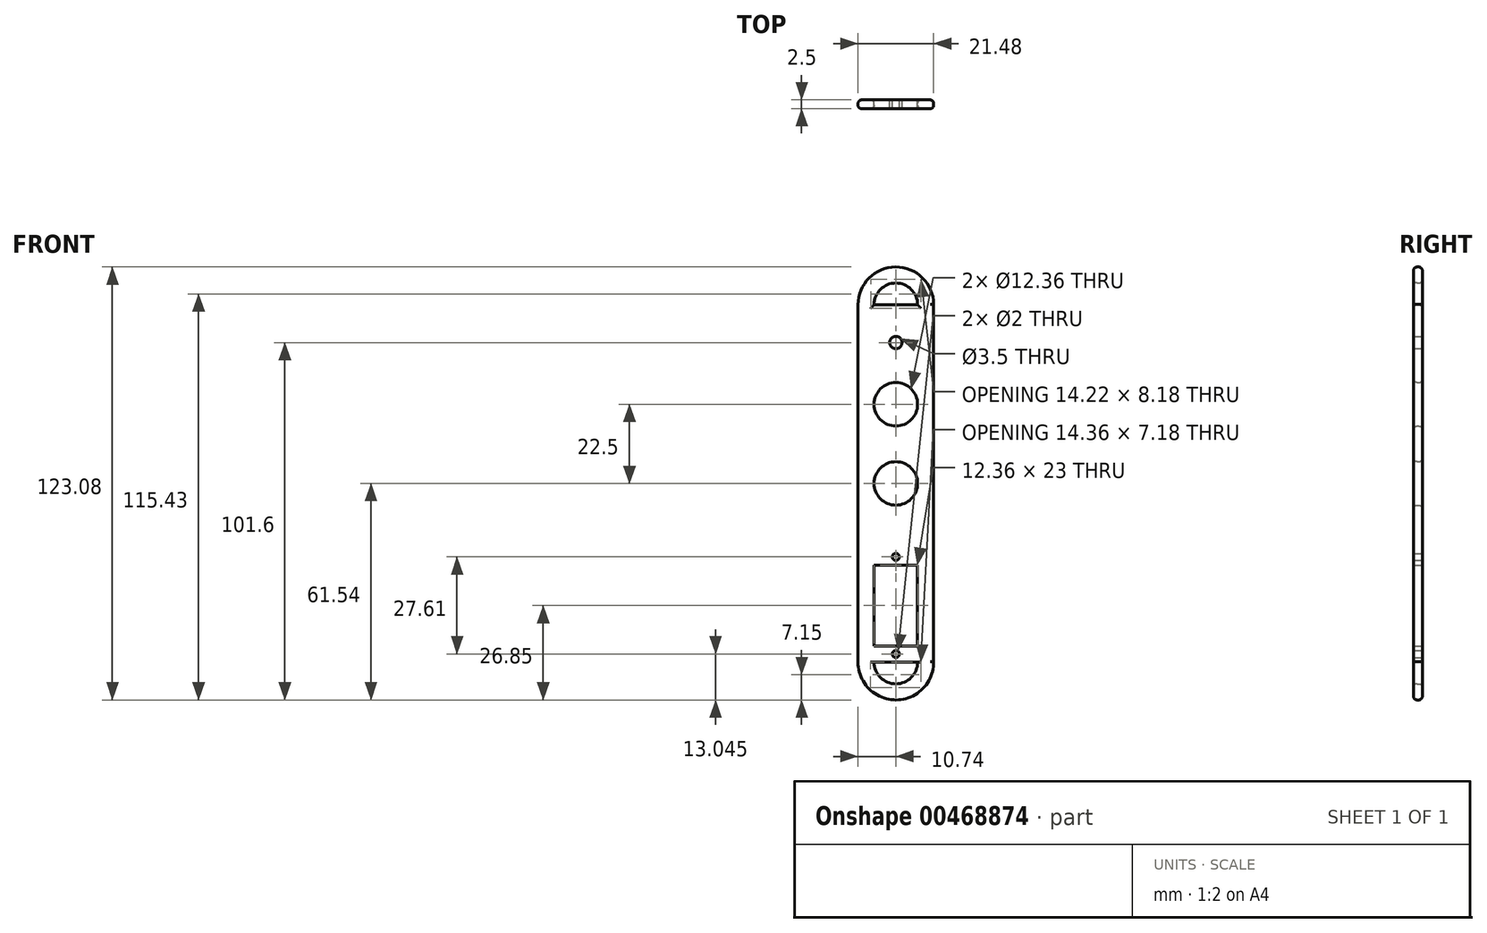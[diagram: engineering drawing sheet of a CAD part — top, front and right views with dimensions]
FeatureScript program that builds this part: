
annotation { "Feature Type Name" : "Feature", "Feature Type Description" : "" }
export const myFeature = defineFeature(function(context is Context, id is Id, definition is map)
    precondition{}
    {
        {
            var Q0;
            Q0=qCreatedBy(makeId("Front.planeOp"),FACE);
            var sketch = newSketch(context, id + "F0", { "sketchPlane" : qUnion([Q0])});
            skPoint(sketch, "E0.middle", {"position": v(0, 0) * mm});
            skLineSegment(sketch, "E1", {"start": v(0, 51) * mm, "end": v(0, 54.51) * mm});
            skArc(sketch, "E2", {"start": v(-6.18, -38.1) * mm, "mid": v(0, -44.28) * mm, "end": v(6.18, -38.1) * mm});
            skArc(sketch, "E3", {"start": v(-10.74, -38.1) * mm, "mid": v(0.07, -48.84) * mm, "end": v(10.74, -37.97) * mm});
            skLineSegment(sketch, "E4", {"start": v(6.18, -38.1) * mm, "end": v(-6.18, -38.1) * mm});
            skLineSegment(sketch, "E5", {"start": v(-6.18, -38.1) * mm, "end": v(-6.18, -38.1) * mm});
            skArc(sketch, "E6", {"start": v(6.18, 63.5) * mm, "mid": v(0, 69.68) * mm, "end": v(-6.18, 63.5) * mm});
            skArc(sketch, "E7", {"start": v(10.74, 63.37) * mm, "mid": v(0.07, 74.24) * mm, "end": v(-10.74, 63.5) * mm});
            skCircle(sketch, "E8", {"center": v(0, 52.76) * mm, "radius": 1.75 * mm});
            skLineSegment(sketch, "E9", {"start": v(6.18, 63.5) * mm, "end": v(-6.18, 63.5) * mm});
            skLineSegment(sketch, "E10", {"start": v(-10.74, 63.5) * mm, "end": v(-10.74, -38.1) * mm});
            skLineSegment(sketch, "E11", {"start": v(10.74, -37.97) * mm, "end": v(10.74, 63.63) * mm});
            skLineSegment(sketch, "E12", {"start": v(6.18, 12.7) * mm, "end": v(-6.18, 12.7) * mm, "construction": true});
            skCircle(sketch, "E13", {"center": v(0, 12.7) * mm, "radius": 6.18 * mm});
            skLineSegment(sketch, "E14", {"start": v(-6.18, -38.1) * mm, "end": v(-6.18, -33.5) * mm, "construction": true});
            skLineSegment(sketch, "E15", {"start": v(6.18, -38.1) * mm, "end": v(6.18, -33.5) * mm, "construction": true});
            skLineSegment(sketch, "E16", {"start": v(-6.18, -33.5) * mm, "end": v(6.18, -33.5) * mm});
            skLineSegment(sketch, "E17", {"start": v(-6.18, -33.5) * mm, "end": v(-6.18, -10.5) * mm});
            skLineSegment(sketch, "E18", {"start": v(-6.18, -10.5) * mm, "end": v(6.18, -10.5) * mm});
            skLineSegment(sketch, "E19", {"start": v(6.18, -10.5) * mm, "end": v(6.18, -33.5) * mm});
            skCircle(sketch, "E20.0.1.0", {"center": v(0, 35.2) * mm, "radius": 6.18 * mm});
            skLineSegment(sketch, "E20.direction1", {"start": v(0, 12.7) * mm, "end": v(25, 12.7) * mm, "construction": true});
            skLineSegment(sketch, "E20.direction2", {"start": v(0, 12.7) * mm, "end": v(0, 35.2) * mm, "construction": true});
            skLineSegment(sketch, "E21", {"start": v(-6.18, -38.1) * mm, "end": v(6.18, -33.5) * mm, "construction": true});
            skLineSegment(sketch, "E22", {"start": v(-6.18, -33.5) * mm, "end": v(6.18, -38.1) * mm, "construction": true});
            skCircle(sketch, "E23", {"center": v(0, -35.8) * mm, "radius": 1 * mm});
            skLineSegment(sketch, "E24", {"start": v(-6.18, -10.5) * mm, "end": v(-6.18, -5.88) * mm, "construction": true});
            skLineSegment(sketch, "E25", {"start": v(6.18, -10.5) * mm, "end": v(6.18, -5.88) * mm, "construction": true});
            skLineSegment(sketch, "E26", {"start": v(-6.18, -5.88) * mm, "end": v(6.18, -5.88) * mm, "construction": true});
            skLineSegment(sketch, "E27", {"start": v(-6.18, -10.5) * mm, "end": v(6.18, -5.88) * mm, "construction": true});
            skLineSegment(sketch, "E28", {"start": v(6.18, -10.5) * mm, "end": v(-6.18, -5.88) * mm, "construction": true});
            skCircle(sketch, "E29", {"center": v(0, -8.19) * mm, "radius": 1 * mm});
            skSolve(sketch);
        }
        {
            var Q0;
            Q0=makeQuery(id+"F0.imprint","IMPRINT",FACE,{"disambiguationData":[TD([[makeQuery(id+"F0.imprint","IMPRINT",EDGE,{"derivedFrom":sQuery(id+"F0.wireOp",EDGE,"E2")}),-1.0]])]});
            extrude(context, id + "F1", {"entities" : qUnion([Q0]), "depth" : 2.5 * mm});
        }
        {
            var Q0;
            Q0=makeQuery(id+"F1.opExtrude","CAP_EDGE",EDGE,{"disambiguationData":[OSD([sQuery(id+"F0.wireOp",EDGE,"E9")])],"isStart":true});
            var Q1;
            Q1=makeQuery(id+"F1.opExtrude","CAP_EDGE",EDGE,{"disambiguationData":[OSD([sQuery(id+"F0.wireOp",EDGE,"E9")])],"isStart":false});
            var Q2;
            Q2=makeQuery(id+"F1.opExtrude","CAP_EDGE",EDGE,{"disambiguationData":[OSD([sQuery(id+"F0.wireOp",EDGE,"E6")])],"isStart":true});
            var Q3;
            Q3=makeQuery(id+"F1.opExtrude","CAP_EDGE",EDGE,{"disambiguationData":[OSD([sQuery(id+"F0.wireOp",EDGE,"E6")])],"isStart":false});
            var Q4;
            Q4=makeQuery(id+"F1.opExtrude","CAP_EDGE",EDGE,{"disambiguationData":[OSD([sQuery(id+"F0.wireOp",EDGE,"E7")])],"isStart":false});
            var Q5;
            Q5=makeQuery(id+"F1.opExtrude","CAP_EDGE",EDGE,{"disambiguationData":[OSD([sQuery(id+"F0.wireOp",EDGE,"E7")])],"isStart":true});
            var Q6;
            Q6=makeQuery(id+"F1.opExtrude","CAP_EDGE",EDGE,{"disambiguationData":[OSD([sQuery(id+"F0.wireOp",EDGE,"E20.0.1.0")])],"isStart":true});
            var Q7;
            Q7=makeQuery(id+"F1.opExtrude","CAP_EDGE",EDGE,{"disambiguationData":[OSD([sQuery(id+"F0.wireOp",EDGE,"E20.0.1.0")])],"isStart":false});
            var Q8;
            Q8=makeQuery(id+"F1.opExtrude","CAP_EDGE",EDGE,{"disambiguationData":[OSD([sQuery(id+"F0.wireOp",EDGE,"E13")])],"isStart":false});
            var Q9;
            Q9=makeQuery(id+"F1.opExtrude","CAP_EDGE",EDGE,{"disambiguationData":[OSD([sQuery(id+"F0.wireOp",EDGE,"E13")])],"isStart":true});
            var Q10;
            Q10=makeQuery(id+"F1.opExtrude","CAP_EDGE",EDGE,{"disambiguationData":[OSD([sQuery(id+"F0.wireOp",EDGE,"E2")])],"isStart":false});
            var Q11;
            Q11=makeQuery(id+"F1.opExtrude","CAP_EDGE",EDGE,{"disambiguationData":[OSD([sQuery(id+"F0.wireOp",EDGE,"E2")])],"isStart":true});
            fillet(context, id + "F2", {"entities" : qUnion([Q0, Q1, Q2, Q3, Q4, Q5, Q6, Q7, Q8, Q9, Q10, Q11]), "radius" : 1 * mm, "tangentPropagation" : true, "allowEdgeOverflow" : false});
        }
    });
